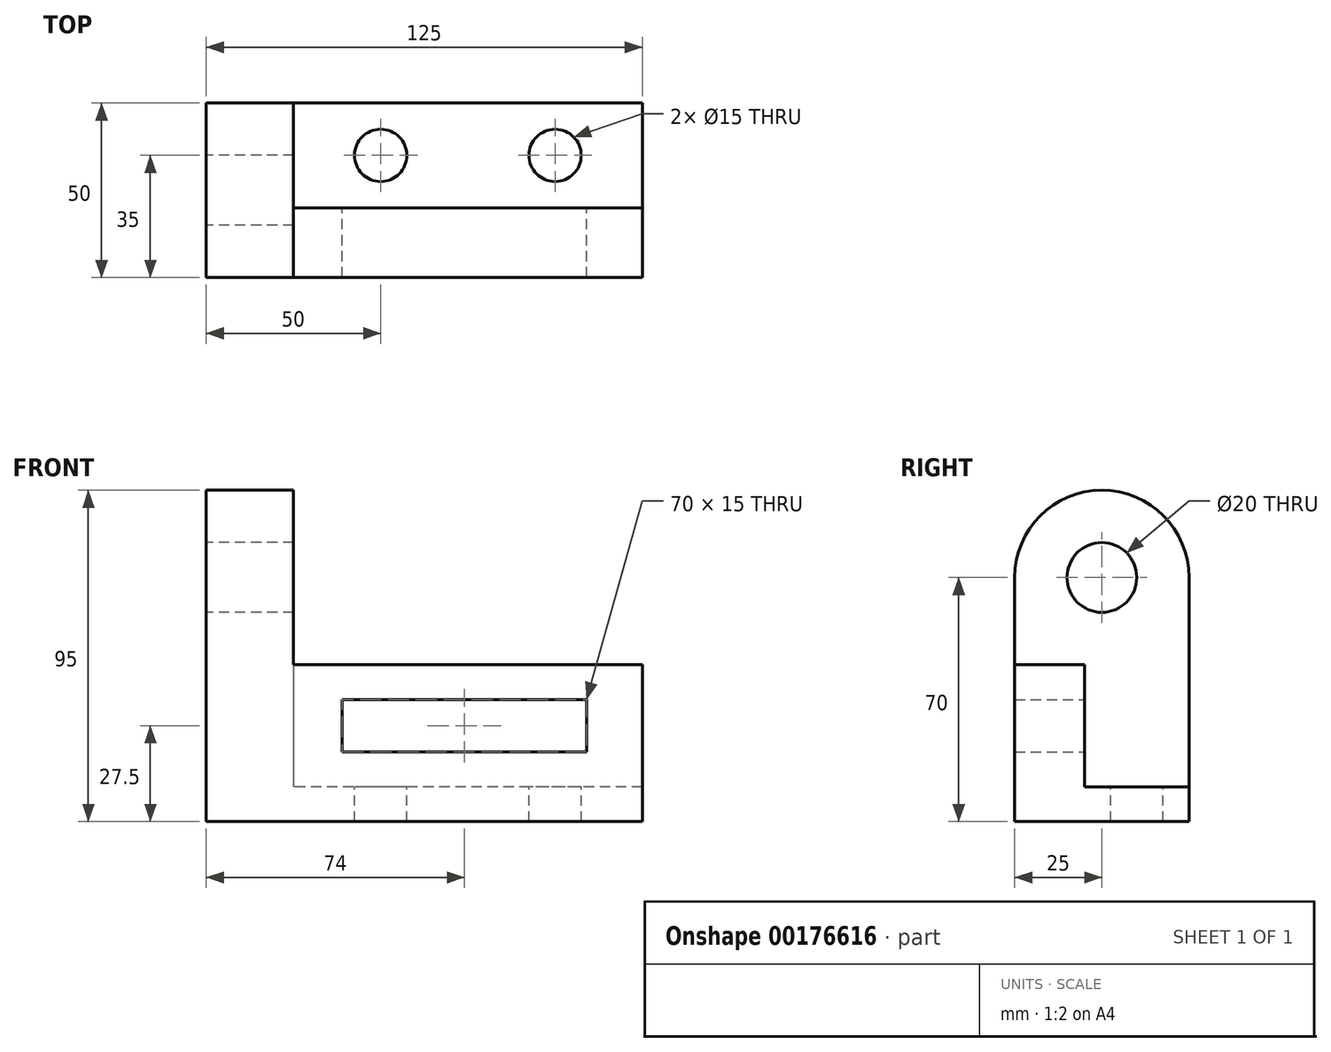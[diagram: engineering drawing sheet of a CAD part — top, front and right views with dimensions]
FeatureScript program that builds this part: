
annotation { "Feature Type Name" : "Feature", "Feature Type Description" : "" }
export const myFeature = defineFeature(function(context is Context, id is Id, definition is map)
    precondition{}
    {
        {
            var Q0;
            Q0=qCreatedBy(makeId("Right.planeOp"),FACE);
            var sketch = newSketch(context, id + "F0", { "sketchPlane" : qUnion([Q0])});
            skLineSegment(sketch, "E0.bottom", {"start": v(0, 0) * mm, "end": v(50, 0) * mm});
            skCircle(sketch, "E1", {"center": v(25, 70) * mm, "radius": 10 * mm});
            skArc(sketch, "E2", {"start": v(25, 95) * mm, "mid": v(7.32, 87.68) * mm, "end": v(0, 70) * mm});
            skArc(sketch, "E3", {"start": v(50, 70) * mm, "mid": v(42.68, 87.68) * mm, "end": v(25, 95) * mm});
            skLineSegment(sketch, "E4", {"start": v(0, 70) * mm, "end": v(0, 0) * mm});
            skLineSegment(sketch, "E5", {"start": v(50, 70) * mm, "end": v(50, 0) * mm});
            skSolve(sketch);
        }
        {
            var Q0;
            Q0 = qSketchRegion(id + "F0", true);
            extrude(context, id + "F1", {"entities" : qUnion([Q0]), "depth" : 25 * mm});
        }
        {
            var Q0;
            Q0=makeQuery(id+"F1.opExtrude","CAP_FACE",FACE,{"disambiguationData":[OSD([sQuery(id+"F0.wireOp",EDGE,"E0.bottom"),sQuery(id+"F0.wireOp",EDGE,"E1"),sQuery(id+"F0.wireOp",EDGE,"E2"),sQuery(id+"F0.wireOp",EDGE,"E3"),sQuery(id+"F0.wireOp",EDGE,"E4"),sQuery(id+"F0.wireOp",EDGE,"E5")])],"isStart":false});
            var sketch = newSketch(context, id + "F2", { "sketchPlane" : qUnion([Q0])});
            skLineSegment(sketch, "E6.bottom", {"start": v(0, 0) * mm, "end": v(50, 0) * mm});
            skLineSegment(sketch, "E6.left", {"start": v(0, 0) * mm, "end": v(0, 45) * mm});
            skLineSegment(sketch, "E7", {"start": v(0, 45) * mm, "end": v(20, 45) * mm});
            skLineSegment(sketch, "E8", {"start": v(20, 45) * mm, "end": v(20, 10) * mm});
            skLineSegment(sketch, "E9", {"start": v(20, 10) * mm, "end": v(50, 10) * mm});
            skLineSegment(sketch, "E10", {"start": v(50, 10) * mm, "end": v(50, 0) * mm});
            skSolve(sketch);
        }
        {
            var Q0;
            Q0 = qSketchRegion(id + "F2", true);
            extrude(context, id + "F3", {"entities" : qUnion([Q0]), "operationType" : NewBodyOperationType.ADD, "depth" : 100 * mm});
        }
        {
            var Q0;
            Q0=makeQuery(id+"F3.opExtrude","SWEPT_FACE",FACE,{"disambiguationData":[OSD([sQuery(id+"F2.wireOp",EDGE,"E8")])]});
            var sketch = newSketch(context, id + "F4", { "sketchPlane" : qUnion([Q0])});
            skLineSegment(sketch, "E11.bottom", {"start": v(-109, 35) * mm, "end": v(-39, 35) * mm});
            skLineSegment(sketch, "E11.top", {"start": v(-109, 20) * mm, "end": v(-39, 20) * mm});
            skLineSegment(sketch, "E11.left", {"start": v(-109, 35) * mm, "end": v(-109, 20) * mm});
            skLineSegment(sketch, "E11.right", {"start": v(-39, 35) * mm, "end": v(-39, 20) * mm});
            skSolve(sketch);
        }
        {
            var Q0;
            Q0 = qSketchRegion(id + "F4", true);
            extrude(context, id + "F5", {"entities" : qUnion([Q0]), "operationType" : NewBodyOperationType.REMOVE, "oppositeDirection" : true, "depth" : 20 * mm});
        }
        {
            var Q0;
            Q0=makeQuery(id+"F3.opExtrude","SWEPT_FACE",FACE,{"disambiguationData":[OSD([sQuery(id+"F2.wireOp",EDGE,"E9")])]});
            var sketch = newSketch(context, id + "F6", { "sketchPlane" : qUnion([Q0])});
            skCircle(sketch, "E12", {"center": v(100, 35) * mm, "radius": 7.5 * mm});
            skCircle(sketch, "E13", {"center": v(50, 35) * mm, "radius": 7.5 * mm});
            skSolve(sketch);
        }
        {
            var Q0;
            Q0 = qSketchRegion(id + "F6", true);
            extrude(context, id + "F7", {"entities" : qUnion([Q0]), "operationType" : NewBodyOperationType.REMOVE, "oppositeDirection" : true, "depth" : 10 * mm});
        }
    });
